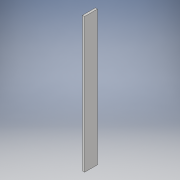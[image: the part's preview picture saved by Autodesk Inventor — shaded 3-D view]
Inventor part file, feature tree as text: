
AUTODESK INVENTOR PART (.ipt)
format: ipt  version: 2017 (Build 210142000, 142)  size: 91,136 bytes
history: native  units: in
note: dims shown in document units (in); Inventor stores cm internally (conversion verified against a paired STEP export)
features: extrude x1, sketch x1
ambient origin geometry x8: Origin, YZ Plane, XZ Plane, XY Plane, X Axis, Y Axis, Z Axis, Center Point
bodies: Solid1 (feature_tree)
feature tree (2):
  extrude  "Extrusion1"  Depth=6.0in
  sketch  "Sketch1"  dims[d0=1.0in d1=6.0in d2=63.0in d3=0.0in]
